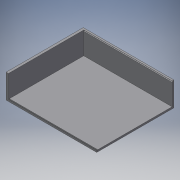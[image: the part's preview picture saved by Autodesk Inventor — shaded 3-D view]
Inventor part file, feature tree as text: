
AUTODESK INVENTOR PART (.ipt)
format: ipt  version: 2016 SP2 (Build 200236200, 236)  size: 114,176 bytes
history: native  units: mm
features: reference x5, extrude x2, sketch x2
ambient origin geometry x8: Origin, YZ Plane, XZ Plane, XY Plane, X Axis, Y Axis, Z Axis, Center Point
bodies: Volumenkörper1 (feature_tree)
feature tree (9):
  extrude  "Extrusion1"  Depth=2.0mm
  extrude  "Extrusion2"  Depth=2.5mm
  sketch  "Skizze1"  dims[d2=0.1mm d4=2.0mm]
  reference  "Referenz1"
  reference  "Referenz2"
  reference  "Referenz3"
  reference  "Referenz4"
  reference  "Referenz5"
  sketch  "Skizze2"  dims[d6=1.1mm d8=0.1mm d9=0.1mm d10=0.15mm d11=2.0mm d12=95.0mm d13=0.0mm d14=2.5mm d15=0.0mm]
